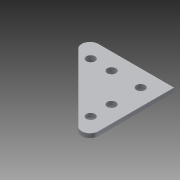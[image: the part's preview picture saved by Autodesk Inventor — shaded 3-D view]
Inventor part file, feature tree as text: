
AUTODESK INVENTOR PART (.ipt)
format: ipt  version: 2014 SP1 (Build 180222100, 222)  size: 105,472 bytes
history: native  units: in
note: dims shown in document units (in); Inventor stores cm internally (conversion verified against a paired STEP export)
features: extrude x1, fillet x1, sketch x1
ambient origin geometry x8: Origin, YZ Plane, XZ Plane, XY Plane, X Axis, Y Axis, Z Axis, Center Point
bodies: Solid1 (feature_tree)
feature tree (3):
  extrude  "Extrusion1"  Depth=2.875in
  fillet  "Fillet1"  Radius=0.5in
  sketch  "Sketch1"  dims[d0=2.875in d1=2.875in d2=0.5in d3=0.5in d4=0.26in d5=0.26in d6=0.26in d7=0.26in d8=0.625in d9=0.625in d10=0.26in d11=0.125in d12=0.0in d13=0.25in d14=1.375in d15=1.375in]
